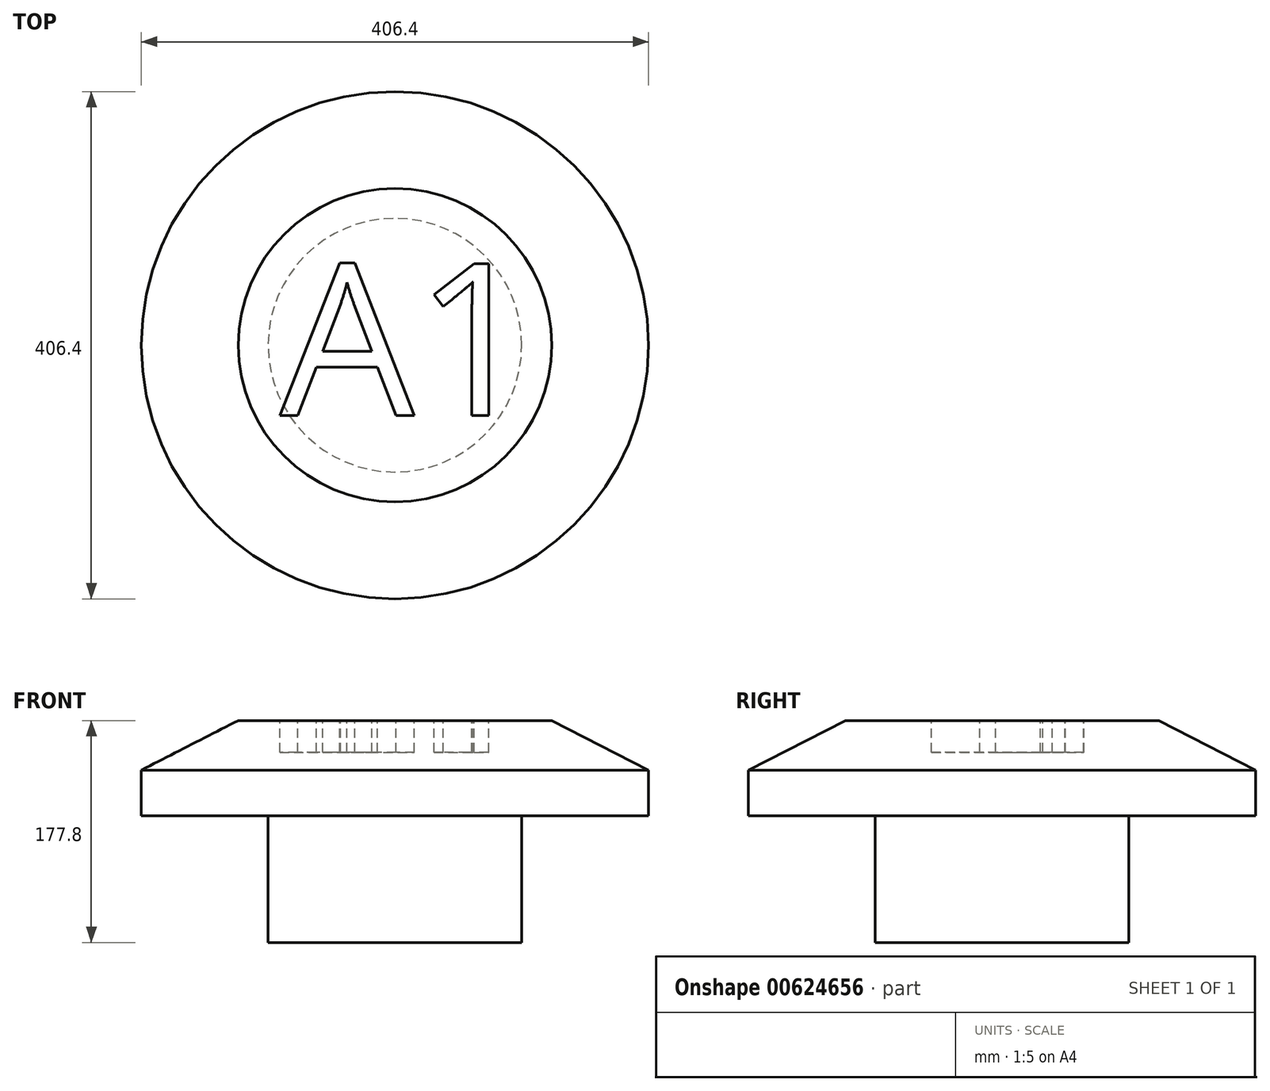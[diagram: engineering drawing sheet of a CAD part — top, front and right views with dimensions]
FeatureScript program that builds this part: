
annotation { "Feature Type Name" : "Feature", "Feature Type Description" : "" }
export const myFeature = defineFeature(function(context is Context, id is Id, definition is map)
    precondition{}
    {
        {
            var Q0;
            Q0=qCreatedBy(makeId("Front.planeOp"),FACE);
            var sketch = newSketch(context, id + "F0", { "sketchPlane" : qUnion([Q0])});
            skLineSegment(sketch, "E0", {"start": v(0, 409.03) * mm, "end": v(0, -413.18) * mm, "construction": true});
            skLineSegment(sketch, "E1", {"start": v(0, 0) * mm, "end": v(-101.6, 0) * mm});
            skLineSegment(sketch, "E2", {"start": v(-101.6, 0) * mm, "end": v(-101.6, 101.6) * mm});
            skLineSegment(sketch, "E3", {"start": v(-101.6, 101.6) * mm, "end": v(-203.2, 101.6) * mm});
            skLineSegment(sketch, "E4", {"start": v(-203.2, 101.6) * mm, "end": v(-203.2, 177.8) * mm});
            skLineSegment(sketch, "E5", {"start": v(-203.2, 177.8) * mm, "end": v(0, 177.8) * mm});
            skLineSegment(sketch, "E6", {"start": v(0, 177.8) * mm, "end": v(0, 0) * mm});
            skSolve(sketch);
        }
        {
            var Q0;
            Q0=makeQuery(id+"F0.imprint","IMPRINT",FACE,{"disambiguationData":[TD([[makeQuery(id+"F0.imprint","IMPRINT",EDGE,{"derivedFrom":sQuery(id+"F0.wireOp",EDGE,"E1")}),-1.0]])]});
            var Q1;
            Q1=sQuery(id+"F0.wireOp",EDGE,"E0");
            revolve(context, id + "F1", {"entities" : qUnion([Q0]), "axis" : qUnion([Q1]), "revolveType" : RevolveType.FULL});
        }
        {
            var Q0;
            Q0=makeQuery(id+"F1.opRevolve","SWEPT_FACE",FACE,{"disambiguationData":[OSD([sQuery(id+"F0.wireOp",EDGE,"E5")])]});
            var sketch = newSketch(context, id + "F2", { "sketchPlane" : qUnion([Q0])});
            skText(sketch, "E7", { "text": "A1", "fontName": "OpenSans-Regular.ttf"});
            const initialGuessF2  = {"E7": [-0.0923, -0.05649, 1, 0, 0.1228]};
            skSetInitialGuess(sketch, initialGuessF2);
            skSolve(sketch);
        }
        {
            var Q0;
            Q0 = qSketchRegion(id + "F2", true);
            extrude(context, id + "F3", {"entities" : qUnion([Q0]), "operationType" : NewBodyOperationType.REMOVE, "oppositeDirection" : true, "depth" : 25.4 * mm, "offsetDistance" : 25.4 * mm});
        }
        {
            var Q0;
            Q0=qCreatedBy(makeId("Front.planeOp"),FACE);
            var sketch = newSketch(context, id + "F4", { "sketchPlane" : qUnion([Q0])});
            skLineSegment(sketch, "E8", {"start": v(-203.77, 137.77) * mm, "end": v(-123.82, 178.68) * mm});
            skLineSegment(sketch, "E9", {"start": v(-123.82, 178.68) * mm, "end": v(-215.33, 184.3) * mm});
            skLineSegment(sketch, "E10", {"start": v(-215.33, 184.3) * mm, "end": v(-203.77, 137.77) * mm});
            skLineSegment(sketch, "E11", {"start": v(0, 0) * mm, "end": v(0, 138.71) * mm, "construction": true});
            skSolve(sketch);
        }
        {
            var Q0;
            Q0 = qSketchRegion(id + "F4", true);
            var Q1;
            Q1=sQuery(id+"F4.wireOp",EDGE,"E11");
            revolve(context, id + "F5", {"operationType" : NewBodyOperationType.REMOVE, "entities" : qUnion([Q0]), "axis" : qUnion([Q1]), "revolveType" : RevolveType.FULL, "oppositeDirection" : true});
        }
    });
